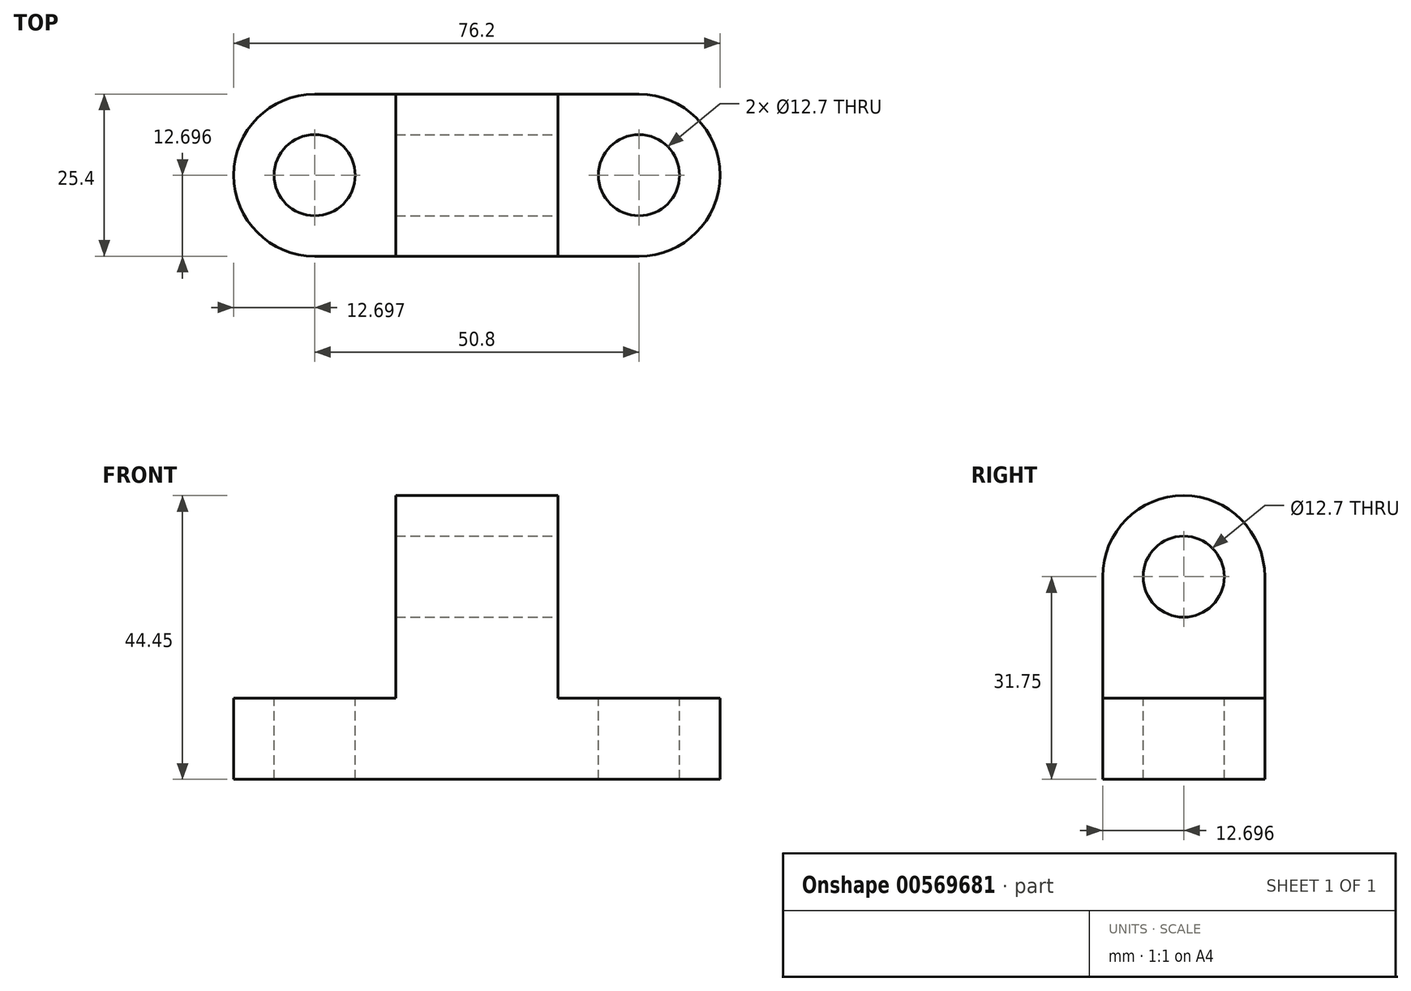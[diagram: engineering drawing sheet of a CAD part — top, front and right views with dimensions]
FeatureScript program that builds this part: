
annotation { "Feature Type Name" : "Feature", "Feature Type Description" : "" }
export const myFeature = defineFeature(function(context is Context, id is Id, definition is map)
    precondition{}
    {
        {
            var Q0;
            Q0=qCreatedBy(makeId("Top.planeOp"),FACE);
            var sketch = newSketch(context, id + "F0", { "sketchPlane" : qUnion([Q0])});
            skLineSegment(sketch, "E0.bottom", {"start": v(-18.9, -23.55) * mm, "end": v(57.3, -23.55) * mm});
            skLineSegment(sketch, "E0.top", {"start": v(-18.9, 1.85) * mm, "end": v(57.3, 1.85) * mm});
            skLineSegment(sketch, "E0.left", {"start": v(-18.9, -23.55) * mm, "end": v(-18.9, 1.85) * mm});
            skLineSegment(sketch, "E0.right", {"start": v(57.3, -23.55) * mm, "end": v(57.3, 1.85) * mm});
            skSolve(sketch);
        }
        {
            var Q0;
            Q0 = qSketchRegion(id + "F0", true);
            extrude(context, id + "F1", {"entities" : qUnion([Q0]), "depth" : 44.45 * mm, "offsetDistance" : 25.4 * mm});
        }
        {
            var Q0;
            Q0=makeQuery(id+"F1.opExtrude","SWEPT_FACE",FACE,{"disambiguationData":[OSD([sQuery(id+"F0.wireOp",EDGE,"E0.bottom")])]});
            var sketch = newSketch(context, id + "F2", { "sketchPlane" : qUnion([Q0])});
            skLineSegment(sketch, "E1", {"start": v(31.9, 44.45) * mm, "end": v(31.9, 12.7) * mm});
            skLineSegment(sketch, "E2", {"start": v(31.9, 12.7) * mm, "end": v(57.3, 12.7) * mm});
            skLineSegment(sketch, "E3", {"start": v(57.3, 12.7) * mm, "end": v(57.3, 44.45) * mm});
            skLineSegment(sketch, "E4", {"start": v(57.3, 44.45) * mm, "end": v(31.9, 44.45) * mm});
            skLineSegment(sketch, "E5", {"start": v(6.5, 44.45) * mm, "end": v(6.5, 12.7) * mm});
            skLineSegment(sketch, "E6", {"start": v(6.5, 12.7) * mm, "end": v(-18.9, 12.7) * mm});
            skLineSegment(sketch, "E7", {"start": v(-18.9, 12.7) * mm, "end": v(-18.9, 44.45) * mm});
            skLineSegment(sketch, "E8", {"start": v(-18.9, 44.45) * mm, "end": v(6.5, 44.45) * mm});
            skSolve(sketch);
        }
        {
            var Q0;
            Q0=makeQuery(id+"F2.imprint","IMPRINT",FACE,{"disambiguationData":[TD([[makeQuery(id+"F2.imprint","IMPRINT",EDGE,{"derivedFrom":sQuery(id+"F2.wireOp",EDGE,"E5")}),-1.0]])]});
            var Q1;
            Q1=makeQuery(id+"F2.imprint","IMPRINT",FACE,{"disambiguationData":[TD([[makeQuery(id+"F2.imprint","IMPRINT",EDGE,{"derivedFrom":sQuery(id+"F2.wireOp",EDGE,"E1")}),1.0]])]});
            extrude(context, id + "F3", {"entities" : qUnion([Q0, Q1]), "operationType" : NewBodyOperationType.REMOVE, "oppositeDirection" : true, "depth" : 25.4 * mm, "offsetDistance" : 25.4 * mm});
        }
        {
            var Q0;
            Q0=makeQuery(id+"F3.boolean.opBoolean","COPY",FACE,{"derivedFrom":makeQuery(id+"F3.opExtrude","SWEPT_FACE",FACE,{"disambiguationData":[OSD([sQuery(id+"F2.wireOp",EDGE,"E2")])]})});
            var sketch = newSketch(context, id + "F4", { "sketchPlane" : qUnion([Q0])});
            skLineSegment(sketch, "E9", {"start": v(57.3, 1.85) * mm, "end": v(44.6, 1.85) * mm});
            skCircle(sketch, "E10", {"center": v(44.6, -10.85) * mm, "radius": 6.35 * mm});
            skPoint(sketch, "E11.orphan", {"position": v(44.6, -23.55) * mm});
            skSolve(sketch);
        }
        {
            var Q0;
            Q0 = qSketchRegion(id + "F4", true);
            extrude(context, id + "F5", {"entities" : qUnion([Q0]), "operationType" : NewBodyOperationType.REMOVE, "oppositeDirection" : true, "depth" : 25.4 * mm, "offsetDistance" : 25.4 * mm});
        }
        {
            var Q0;
            Q0=makeQuery(id+"F3.boolean.opBoolean","COPY",FACE,{"derivedFrom":makeQuery(id+"F3.opExtrude","SWEPT_FACE",FACE,{"disambiguationData":[OSD([sQuery(id+"F2.wireOp",EDGE,"E6")])]})});
            var sketch = newSketch(context, id + "F6", { "sketchPlane" : qUnion([Q0])});
            skLineSegment(sketch, "E12", {"start": v(-6.2, -4.5) * mm, "end": v(-6.2, -10.85) * mm});
            skCircle(sketch, "E13", {"center": v(-6.2, -10.85) * mm, "radius": 6.35 * mm});
            skPoint(sketch, "E14.orphan", {"position": v(-6.2, -23.55) * mm});
            skPoint(sketch, "E15.orphan", {"position": v(-6.2, 1.85) * mm});
            skSolve(sketch);
        }
        {
            var Q0;
            Q0 = qSketchRegion(id + "F6", true);
            extrude(context, id + "F7", {"entities" : qUnion([Q0]), "operationType" : NewBodyOperationType.REMOVE, "oppositeDirection" : true, "depth" : 25.4 * mm, "offsetDistance" : 25.4 * mm});
        }
        {
            var Q0;
            Q0=makeQuery(id+"F3.boolean.opBoolean","COPY",FACE,{"derivedFrom":makeQuery(id+"F3.opExtrude","SWEPT_FACE",FACE,{"disambiguationData":[OSD([sQuery(id+"F2.wireOp",EDGE,"E2")])]})});
            var sketch = newSketch(context, id + "F8", { "sketchPlane" : qUnion([Q0])});
            skArc(sketch, "E16", {"start": v(44.6, -23.55) * mm, "mid": v(57.3, -10.85) * mm, "end": v(44.6, 1.85) * mm});
            skSolve(sketch);
        }
        {
            var Q0;
            {var subQ0=sQuery(id+"F8.wireOp",EDGE,"E16");var subQ1=sQuery(id+"F2.wireOp",EDGE,"E2");var subQ2=makeQuery(id+"F3.boolean.opBoolean","COPY",EDGE,{"derivedFrom":makeQuery(id+"F3.opExtrude","CAP_EDGE",EDGE,{"disambiguationData":[OSD([subQ1])],"isStart":false})});var subQ3=makeQuery(id+"F8.imprint","INTERSECT",VERTEX,{"derivedFrom":[subQ2,subQ0]});Q0=makeQuery(id+"F8.imprint","IMPRINT",FACE,{"disambiguationData":[TD([[makeQuery(id+"F8.imprint","IMPRINT",EDGE,{"disambiguationData":[TD([[subQ3,1.0]])],"derivedFrom":subQ0}),-1.0]])]});}
            var Q1;
            {var subQ0=sQuery(id+"F8.wireOp",EDGE,"E16");var subQ1=sQuery(id+"F2.wireOp",EDGE,"E2");var subQ2=makeQuery(id+"F3.boolean.opBoolean","COPY",EDGE,{"derivedFrom":makeQuery(id+"F3.opExtrude","CAP_EDGE",EDGE,{"disambiguationData":[OSD([subQ1])],"isStart":true})});var subQ3=makeQuery(id+"F8.imprint","INTERSECT",VERTEX,{"derivedFrom":[subQ2,subQ0]});Q1=makeQuery(id+"F8.imprint","IMPRINT",FACE,{"disambiguationData":[TD([[makeQuery(id+"F8.imprint","IMPRINT",EDGE,{"disambiguationData":[TD([[subQ3,-1.0]])],"derivedFrom":subQ0}),-1.0]])]});}
            extrude(context, id + "F9", {"entities" : qUnion([Q0, Q1]), "operationType" : NewBodyOperationType.REMOVE, "oppositeDirection" : true, "depth" : 25.4 * mm, "offsetDistance" : 25.4 * mm});
        }
        {
            var Q0;
            Q0=makeQuery(id+"F3.boolean.opBoolean","COPY",FACE,{"derivedFrom":makeQuery(id+"F3.opExtrude","SWEPT_FACE",FACE,{"disambiguationData":[OSD([sQuery(id+"F2.wireOp",EDGE,"E6")])]})});
            var sketch = newSketch(context, id + "F10", { "sketchPlane" : qUnion([Q0])});
            skArc(sketch, "E17", {"start": v(-6.2, 1.85) * mm, "mid": v(-18.9, -10.85) * mm, "end": v(-6.2, -23.55) * mm});
            skSolve(sketch);
        }
        {
            var Q0;
            {var subQ0=sQuery(id+"F10.wireOp",EDGE,"E17");var subQ1=sQuery(id+"F2.wireOp",EDGE,"E6");var subQ2=makeQuery(id+"F3.boolean.opBoolean","COPY",EDGE,{"derivedFrom":makeQuery(id+"F3.opExtrude","CAP_EDGE",EDGE,{"disambiguationData":[OSD([subQ1])],"isStart":true})});var subQ3=makeQuery(id+"F10.imprint","INTERSECT",VERTEX,{"derivedFrom":[subQ2,subQ0]});Q0=makeQuery(id+"F10.imprint","IMPRINT",FACE,{"disambiguationData":[TD([[makeQuery(id+"F10.imprint","IMPRINT",EDGE,{"disambiguationData":[TD([[subQ3,1.0]])],"derivedFrom":subQ0}),-1.0]])]});}
            var Q1;
            {var subQ0=sQuery(id+"F10.wireOp",EDGE,"E17");var subQ1=sQuery(id+"F2.wireOp",EDGE,"E6");var subQ2=makeQuery(id+"F3.boolean.opBoolean","COPY",EDGE,{"derivedFrom":makeQuery(id+"F3.opExtrude","CAP_EDGE",EDGE,{"disambiguationData":[OSD([subQ1])],"isStart":false})});var subQ3=makeQuery(id+"F10.imprint","INTERSECT",VERTEX,{"derivedFrom":[subQ2,subQ0]});Q1=makeQuery(id+"F10.imprint","IMPRINT",FACE,{"disambiguationData":[TD([[makeQuery(id+"F10.imprint","IMPRINT",EDGE,{"disambiguationData":[TD([[subQ3,-1.0]])],"derivedFrom":subQ0}),-1.0]])]});}
            extrude(context, id + "F11", {"entities" : qUnion([Q0, Q1]), "operationType" : NewBodyOperationType.REMOVE, "oppositeDirection" : true, "depth" : 25.4 * mm, "offsetDistance" : 25.4 * mm});
        }
        {
            var Q0;
            Q0=makeQuery(id+"F3.boolean.opBoolean","COPY",FACE,{"derivedFrom":makeQuery(id+"F3.opExtrude","SWEPT_FACE",FACE,{"disambiguationData":[OSD([sQuery(id+"F2.wireOp",EDGE,"E1")])]})});
            var sketch = newSketch(context, id + "F12", { "sketchPlane" : qUnion([Q0])});
            skLineSegment(sketch, "E18", {"start": v(-17.2, 31.75) * mm, "end": v(-4.5, 31.75) * mm});
            skCircle(sketch, "E19", {"center": v(-10.85, 31.75) * mm, "radius": 6.35 * mm});
            skPoint(sketch, "E20.orphan", {"position": v(-23.55, 31.75) * mm});
            skPoint(sketch, "E21.orphan", {"position": v(1.85, 31.75) * mm});
            skSolve(sketch);
        }
        {
            var Q0;
            {var subQ0=sQuery(id+"F12.wireOp",EDGE,"E18");Q0=makeQuery(id+"F12.imprint","IMPRINT",FACE,{"disambiguationData":[TD([[makeQuery(id+"F12.imprint","IMPRINT",EDGE,{"derivedFrom":subQ0}),-1.0]])]});}
            var Q1;
            {var subQ0=sQuery(id+"F12.wireOp",EDGE,"E18");Q1=makeQuery(id+"F12.imprint","IMPRINT",FACE,{"disambiguationData":[TD([[makeQuery(id+"F12.imprint","IMPRINT",EDGE,{"derivedFrom":subQ0}),1.0]])]});}
            extrude(context, id + "F13", {"entities" : qUnion([Q0, Q1]), "operationType" : NewBodyOperationType.REMOVE, "oppositeDirection" : true, "depth" : 25.4 * mm, "offsetDistance" : 25.4 * mm});
        }
        {
            var Q0;
            Q0=makeQuery(id+"F3.boolean.opBoolean","COPY",FACE,{"derivedFrom":makeQuery(id+"F3.opExtrude","SWEPT_FACE",FACE,{"disambiguationData":[OSD([sQuery(id+"F2.wireOp",EDGE,"E1")])]})});
            var sketch = newSketch(context, id + "F14", { "sketchPlane" : qUnion([Q0])});
            skArc(sketch, "E22", {"start": v(1.85, 31.75) * mm, "mid": v(-10.85, 44.45) * mm, "end": v(-23.55, 31.75) * mm});
            skSolve(sketch);
        }
        {
            var Q0;
            {var subQ0=sQuery(id+"F14.wireOp",EDGE,"E22");var subQ1=sQuery(id+"F2.wireOp",EDGE,"E1");var subQ2=makeQuery(id+"F3.boolean.opBoolean","COPY",EDGE,{"derivedFrom":makeQuery(id+"F3.opExtrude","CAP_EDGE",EDGE,{"disambiguationData":[OSD([subQ1])],"isStart":true})});var subQ3=makeQuery(id+"F14.imprint","INTERSECT",VERTEX,{"derivedFrom":[subQ2,subQ0]});Q0=makeQuery(id+"F14.imprint","IMPRINT",FACE,{"disambiguationData":[TD([[makeQuery(id+"F14.imprint","IMPRINT",EDGE,{"disambiguationData":[TD([[subQ3,1.0]])],"derivedFrom":subQ0}),-1.0]])]});}
            var Q1;
            {var subQ0=sQuery(id+"F14.wireOp",EDGE,"E22");var subQ1=sQuery(id+"F2.wireOp",EDGE,"E1");var subQ2=makeQuery(id+"F3.boolean.opBoolean","COPY",EDGE,{"derivedFrom":makeQuery(id+"F3.opExtrude","CAP_EDGE",EDGE,{"disambiguationData":[OSD([subQ1])],"isStart":false})});var subQ3=makeQuery(id+"F14.imprint","INTERSECT",VERTEX,{"derivedFrom":[subQ2,subQ0]});Q1=makeQuery(id+"F14.imprint","IMPRINT",FACE,{"disambiguationData":[TD([[makeQuery(id+"F14.imprint","IMPRINT",EDGE,{"disambiguationData":[TD([[subQ3,-1.0]])],"derivedFrom":subQ0}),-1.0]])]});}
            extrude(context, id + "F15", {"entities" : qUnion([Q0, Q1]), "operationType" : NewBodyOperationType.REMOVE, "oppositeDirection" : true, "depth" : 25.4 * mm, "offsetDistance" : 25.4 * mm});
        }
    });
